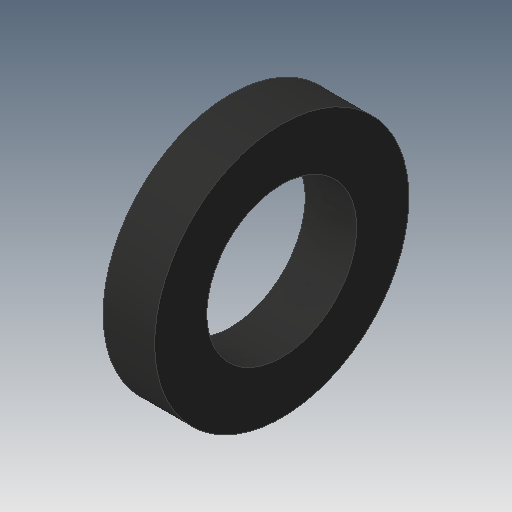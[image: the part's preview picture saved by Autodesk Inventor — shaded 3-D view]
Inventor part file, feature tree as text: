
AUTODESK INVENTOR PART (.ipt)
format: ipt  version: 2018 (Build 220112000, 112)  size: 94,208 bytes
history: native  units: in
note: dims shown in document units (in); Inventor stores cm internally (conversion verified against a paired STEP export)
features: other x3, sketch x1
ambient origin geometry x8: Origin, YZ Plane, XZ Plane, XY Plane, X Axis, Y Axis, Z Axis, Center Point
bodies: Solid1 (feature_tree)
feature tree (4):
  other  "Tire_MIR.ipt"
  other  "Solid1::Tire_MIR.ipt"
  other  "TaggingFeature1"
  sketch  "Sketch1"  dims[d0=0.3937in]
